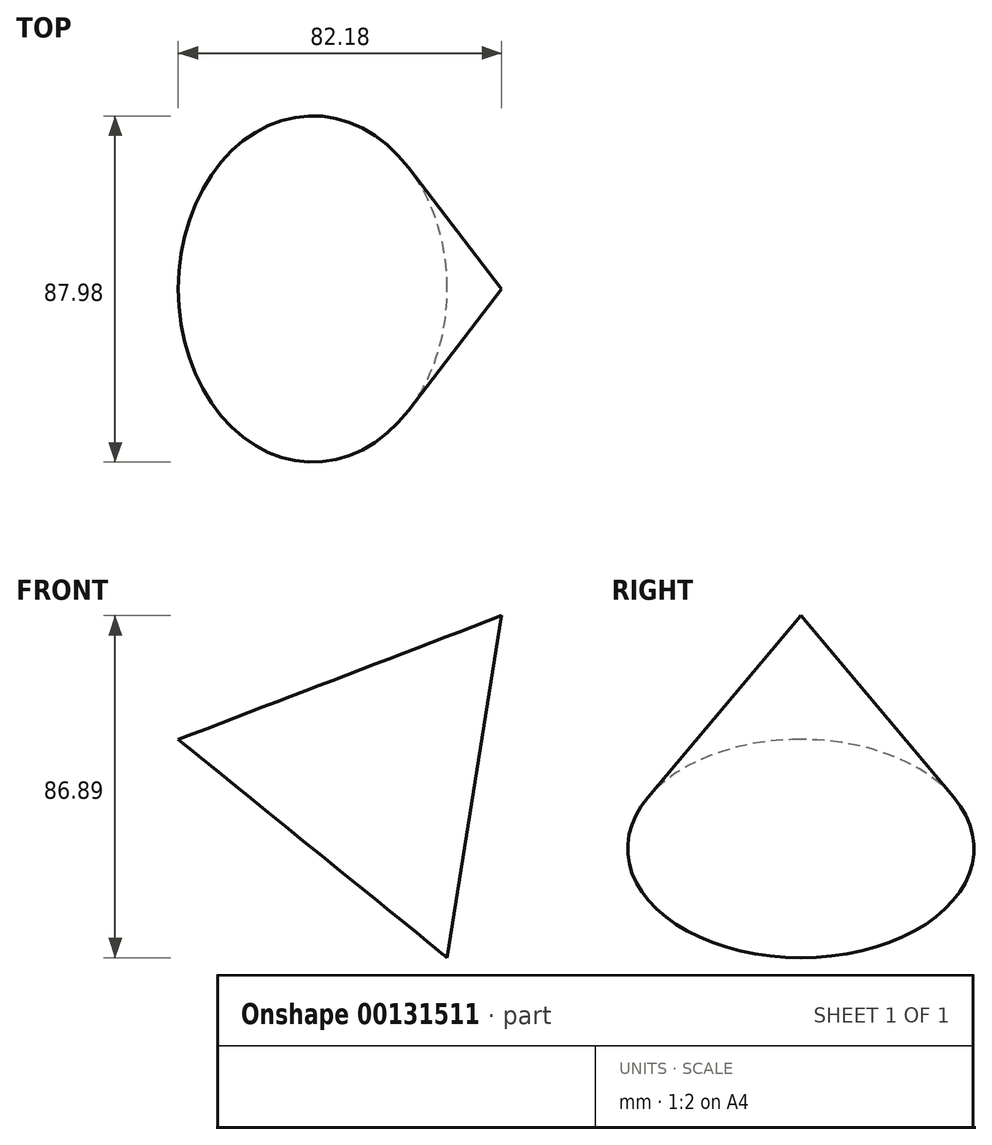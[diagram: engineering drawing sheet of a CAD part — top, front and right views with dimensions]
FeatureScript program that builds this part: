
annotation { "Feature Type Name" : "Feature", "Feature Type Description" : "" }
export const myFeature = defineFeature(function(context is Context, id is Id, definition is map)
    precondition{}
    {
        {
            var Q0;
            Q0=qCreatedBy(makeId("Front.planeOp"),FACE);
            var sketch = newSketch(context, id + "F0", { "sketchPlane" : qUnion([Q0])});
            skCircle(sketch, "E0.cCircle", {"center": v(0, 0) * mm, "radius": 50.8 * mm, "construction": true});
            skLineSegment(sketch, "E0.0", {"start": v(-50.17, 8) * mm, "end": v(32, 39.45) * mm});
            skLineSegment(sketch, "E0.1", {"start": v(32, 39.45) * mm, "end": v(18.16, -47.44) * mm});
            skLineSegment(sketch, "E0.2", {"start": v(18.16, -47.44) * mm, "end": v(-50.17, 8) * mm});
            skLineSegment(sketch, "E1", {"start": v(32, 39.45) * mm, "end": v(-16, -19.72) * mm});
            skSolve(sketch);
        }
        {
            var Q0;
            {var subQ0=sQuery(id+"F0.wireOp",EDGE,"E0.0");Q0=makeQuery(id+"F0.imprint","IMPRINT",FACE,{"disambiguationData":[TD([[makeQuery(id+"F0.imprint","IMPRINT",EDGE,{"derivedFrom":subQ0}),-1.0]])]});}
            var Q1;
            Q1=sQuery(id+"F0.wireOp",EDGE,"E1");
            revolve(context, id + "F1", {"entities" : qUnion([Q0]), "axis" : qUnion([Q1]), "revolveType" : RevolveType.FULL});
        }
    });
